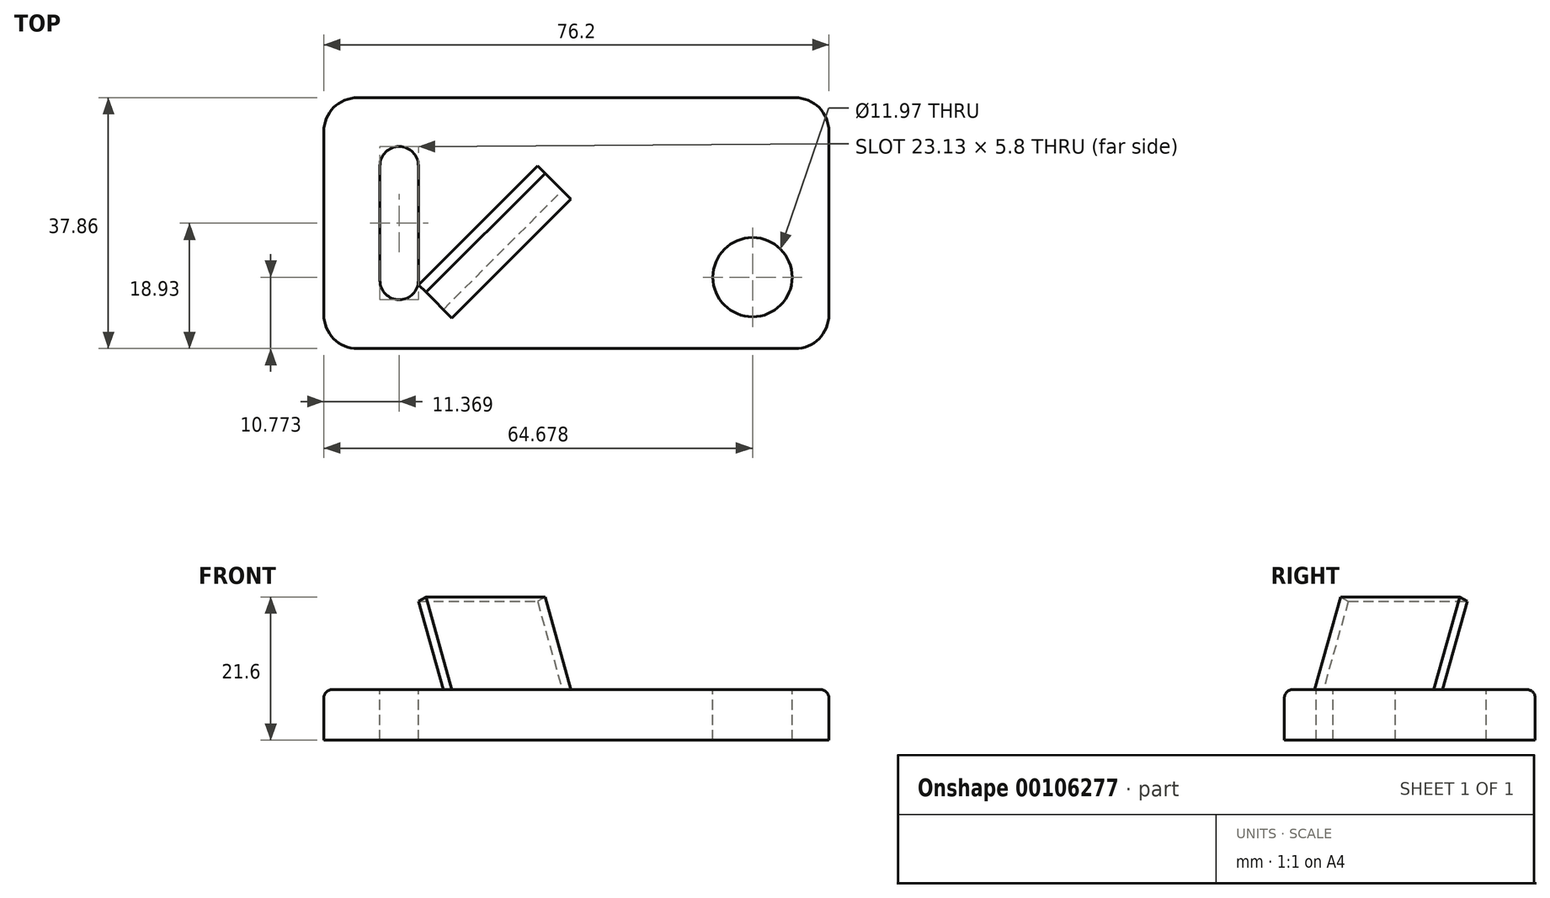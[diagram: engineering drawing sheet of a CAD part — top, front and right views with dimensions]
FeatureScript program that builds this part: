
annotation { "Feature Type Name" : "Feature", "Feature Type Description" : "" }
export const myFeature = defineFeature(function(context is Context, id is Id, definition is map)
    precondition{}
    {
        {
            var Q0;
            Q0=qCreatedBy(makeId("Top.planeOp"),FACE);
            var sketch = newSketch(context, id + "F0", { "sketchPlane" : qUnion([Q0])});
            skLineSegment(sketch, "E0.bottom", {"start": v(38.1, 18.93) * mm, "end": v(-38.1, 18.93) * mm});
            skLineSegment(sketch, "E0.top", {"start": v(38.1, -18.93) * mm, "end": v(-38.1, -18.93) * mm});
            skLineSegment(sketch, "E0.left", {"start": v(38.1, 18.93) * mm, "end": v(38.1, -18.93) * mm});
            skLineSegment(sketch, "E0.right", {"start": v(-38.1, 18.93) * mm, "end": v(-38.1, -18.93) * mm});
            skPoint(sketch, "E0.middle", {"position": v(0, 0) * mm});
            skSolve(sketch);
        }
        {
            var Q0;
            Q0 = qSketchRegion(id + "F0", true);
            extrude(context, id + "F1", {"entities" : qUnion([Q0]), "depth" : 7.62 * mm});
        }
        {
            var Q0;
            Q0=makeQuery(id+"F1.opExtrude","CAP_EDGE",EDGE,{"disambiguationData":[OSD([sQuery(id+"F0.wireOp",EDGE,"E0.right")])],"isStart":false});
            var Q1;
            Q1=makeQuery(id+"F1.opExtrude","CAP_EDGE",EDGE,{"disambiguationData":[OSD([sQuery(id+"F0.wireOp",EDGE,"E0.bottom")])],"isStart":false});
            var Q2;
            Q2=makeQuery(id+"F1.opExtrude","CAP_EDGE",EDGE,{"disambiguationData":[OSD([sQuery(id+"F0.wireOp",EDGE,"E0.left")])],"isStart":false});
            var Q3;
            Q3=makeQuery(id+"F1.opExtrude","CAP_EDGE",EDGE,{"disambiguationData":[OSD([sQuery(id+"F0.wireOp",EDGE,"E0.top")])],"isStart":false});
            fillet(context, id + "F2", {"entities" : qUnion([Q0, Q1, Q2, Q3]), "radius" : 1.27 * mm, "tangentPropagation" : true, "allowEdgeOverflow" : false});
        }
        {
            var Q0;
            Q0=makeQuery(id+"F1.opExtrude","SWEPT_EDGE",EDGE,{"disambiguationData":[OSD([sQuery(id+"F0.wireOp",EDGE,"E0.top"),sQuery(id+"F0.wireOp",EDGE,"E0.right")])]});
            var Q1;
            Q1=makeQuery(id+"F1.opExtrude","SWEPT_EDGE",EDGE,{"disambiguationData":[OSD([sQuery(id+"F0.wireOp",EDGE,"E0.bottom"),sQuery(id+"F0.wireOp",EDGE,"E0.right")])]});
            var Q2;
            Q2=makeQuery(id+"F1.opExtrude","SWEPT_EDGE",EDGE,{"disambiguationData":[OSD([sQuery(id+"F0.wireOp",EDGE,"E0.bottom"),sQuery(id+"F0.wireOp",EDGE,"E0.left")])]});
            var Q3;
            Q3=makeQuery(id+"F1.opExtrude","SWEPT_EDGE",EDGE,{"disambiguationData":[OSD([sQuery(id+"F0.wireOp",EDGE,"E0.top"),sQuery(id+"F0.wireOp",EDGE,"E0.left")])]});
            fillet(context, id + "F3", {"entities" : qUnion([Q0, Q1, Q2, Q3]), "radius" : 5.08 * mm, "tangentPropagation" : true, "allowEdgeOverflow" : false});
        }
        {
            var Q0;
            Q0=makeQuery(id+"F1.opExtrude","CAP_FACE",FACE,{"disambiguationData":[OSD([sQuery(id+"F0.wireOp",EDGE,"E0.bottom"),sQuery(id+"F0.wireOp",EDGE,"E0.top"),sQuery(id+"F0.wireOp",EDGE,"E0.left"),sQuery(id+"F0.wireOp",EDGE,"E0.right")])],"isStart":false});
            var sketch = newSketch(context, id + "F4", { "sketchPlane" : qUnion([Q0])});
            skLineSegment(sketch, "E1", {"start": v(-29.63, 0) * mm, "end": v(-29.63, 8.67) * mm});
            skLineSegment(sketch, "E2", {"start": v(-23.83, 8.67) * mm, "end": v(-23.83, 0) * mm});
            skLineSegment(sketch, "E3.MirrorCS", {"start": v(-29.63, 0) * mm, "end": v(-29.63, -8.67) * mm});
            skLineSegment(sketch, "E4.MirrorCS", {"start": v(-23.83, -8.67) * mm, "end": v(-23.83, 0) * mm});
            skArc(sketch, "E5", {"start": v(-23.83, 8.67) * mm, "mid": v(-26.73, 11.57) * mm, "end": v(-29.63, 8.67) * mm});
            skArc(sketch, "E6", {"start": v(-29.63, -8.67) * mm, "mid": v(-26.73, -11.57) * mm, "end": v(-23.83, -8.67) * mm});
            skPoint(sketch, "E7.MirrorCS.start.orphan", {"position": v(-29.63, -8.67) * mm});
            skSolve(sketch);
        }
        {
            var Q0;
            Q0 = qSketchRegion(id + "F4", true);
            extrude(context, id + "F5", {"entities" : qUnion([Q0]), "operationType" : NewBodyOperationType.REMOVE, "oppositeDirection" : true, "depth" : 25.4 * mm});
        }
        {
            var Q0;
            Q0=makeQuery(id+"F1.opExtrude","CAP_FACE",FACE,{"disambiguationData":[OSD([sQuery(id+"F0.wireOp",EDGE,"E0.bottom"),sQuery(id+"F0.wireOp",EDGE,"E0.top"),sQuery(id+"F0.wireOp",EDGE,"E0.left"),sQuery(id+"F0.wireOp",EDGE,"E0.right")])],"isStart":false});
            var sketch = newSketch(context, id + "F6", { "sketchPlane" : qUnion([Q0])});
            skCircle(sketch, "E8", {"center": v(26.58, -8.16) * mm, "radius": 5.98 * mm});
            skSolve(sketch);
        }
        {
            var Q0;
            Q0 = qSketchRegion(id + "F6", true);
            extrude(context, id + "F7", {"entities" : qUnion([Q0]), "operationType" : NewBodyOperationType.REMOVE, "oppositeDirection" : true, "depth" : 25.4 * mm});
        }
        {
            var Q0;
            Q0=makeQuery(id+"F5.boolean.opBoolean","COPY",EDGE,{"derivedFrom":makeQuery(id+"F5.opExtrude","SWEPT_EDGE",EDGE,{"disambiguationData":[OSD([sQuery(id+"F4.wireOp",EDGE,"E2"),sQuery(id+"F4.wireOp",EDGE,"E5")])]})});
            cPlane(context, id + "F8", {"entities" : qUnion([Q0]), "cplaneType" : CPlaneType.LINE_ANGLE, "offset" : 25.4 * mm, "angle" : 45 * degree, "width" : 152.4 * mm, "height" : 152.4 * mm});
        }
        {
            var Q0;
            Q0=qCreatedBy(id+"F8.planeOp",FACE);
            var sketch = newSketch(context, id + "F9", { "sketchPlane" : qUnion([Q0])});
            skLineSegment(sketch, "E9", {"start": v(10.28, 20.96) * mm, "end": v(4.98, 7.62) * mm});
            skLineSegment(sketch, "E10", {"start": v(4.98, 7.62) * mm, "end": v(3.12, 7.62) * mm});
            skLineSegment(sketch, "E11", {"start": v(3.12, 7.62) * mm, "end": v(8.67, 21.6) * mm});
            skLineSegment(sketch, "E12", {"start": v(8.67, 21.6) * mm, "end": v(10.28, 20.96) * mm});
            skSolve(sketch);
        }
        {
            var Q0;
            Q0 = qSketchRegion(id + "F9", true);
            extrude(context, id + "F10", {"entities" : qUnion([Q0]), "operationType" : NewBodyOperationType.ADD, "endBound" : BoundingType.SYMMETRIC, "oppositeDirection" : true, "depth" : 25.4 * mm});
        }
    });
